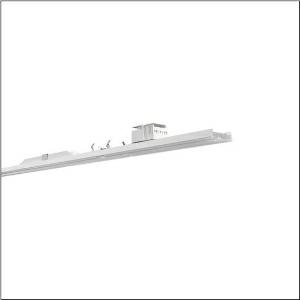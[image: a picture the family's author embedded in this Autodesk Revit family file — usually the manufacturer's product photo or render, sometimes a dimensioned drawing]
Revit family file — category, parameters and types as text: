
# Revit family: licross_r__21_recessed_mo_52tl19dnd75f_c119
name_source: partatom
category: Lighting Fixtures
units: mm (PartAtom-declared; Revit-internal decimal feet)

## family parameters
Cut with Voids When Loaded = No
Host = Face
Light Source = No
Part Type = Normal
Room Calculation Point = No
Round Connector Dimension = Use Diameter
Shared = No

## types (1)
- --- (1 x LED, 7630 lm, 61.1 W, 4000K)
    Apparent Load = 61 VA
    CIE Flux Codes = 55 90 98 100 100
    Color Rendering = 90
    Color Temperature = 4000K
    Default Elevation = 1800 mm
    Description = Licross® 21 Recessed MO, luminaire insert, of sheet steel, galvanised, coil coated, white, length: 1.500mm, width: 66mm, height: 67mm, LED rated luminous flux: 7.630lm, light colour: 940, control gear: DALI 2, control gear: ECG DALI, with plug, 5-pole, with phase selection, mains connection: 220..240V, AC, 50/60Hz, halogen-free wiring, primary light control with lens, of plastic, primary optical cover: cover, of PMMA, light emission: direct distribution, primary light characteristic: double asymmetric, protection rating (complete): IP40, insulation class (complete): insulation class I (protective earthing), certification: CE, ENEC, VDE, UKCA, protection symbol: D if used in an environment without relevant dust loads with corresponding accessories, permissible ambient temperature for indoor applications: -25..+35°C, corresponds to IFS (International Featured Standards) requirements for safety and quality in the food industry, reducing of maximum allowable ambient temperature of 5°C with ceiling mounting, packaging unit: 1 piece
    Height = 58 mm
    Lamp = 1 x LED
    Lamp Light Flux = 7630 lm
    Lamp Power = 61.1 W
    Lamp count = 1
    Length = 1500 mm
    Luminous efficacy = 125 lm/W
    Manufacturer = Siteco
    ModVariant = No
    Model = 52TL19DND75F
    Mounting Place = Ceiling
    Mounting Type = Pendant
    Number of Poles = 1
    OnlyDefault = Yes
    Power Factor = 1
    Product Name = Licross® 21 Recessed MO
    Product group = luminaire insert
    ProductGroupID = 902
    Protection Class = Protection class I
    Protection Degree = IP 40
    RLX_Detail_Level = 1
    RlxData = <blob elided: 22477 chars, md5=08e42279>
    Socket = socket
    Standby Power = 0 W
    System Light Flux = 7630 lm
    System Power = 61 W
    Type Comments = factory setting: luminous flux: 100 % | dim-lin: 254 | 405 mA
    Type Image = l_1266722.jpg
    URL = http://relux.com
    VarID = @adj_129281
    Voltage = 0 V
    Weight = 0.00 kg
    Width = 66 mm

## geometry (parser evidence)
native form markers: Blend x4, Sweep x9
no freeform markers — native parametric forms only
